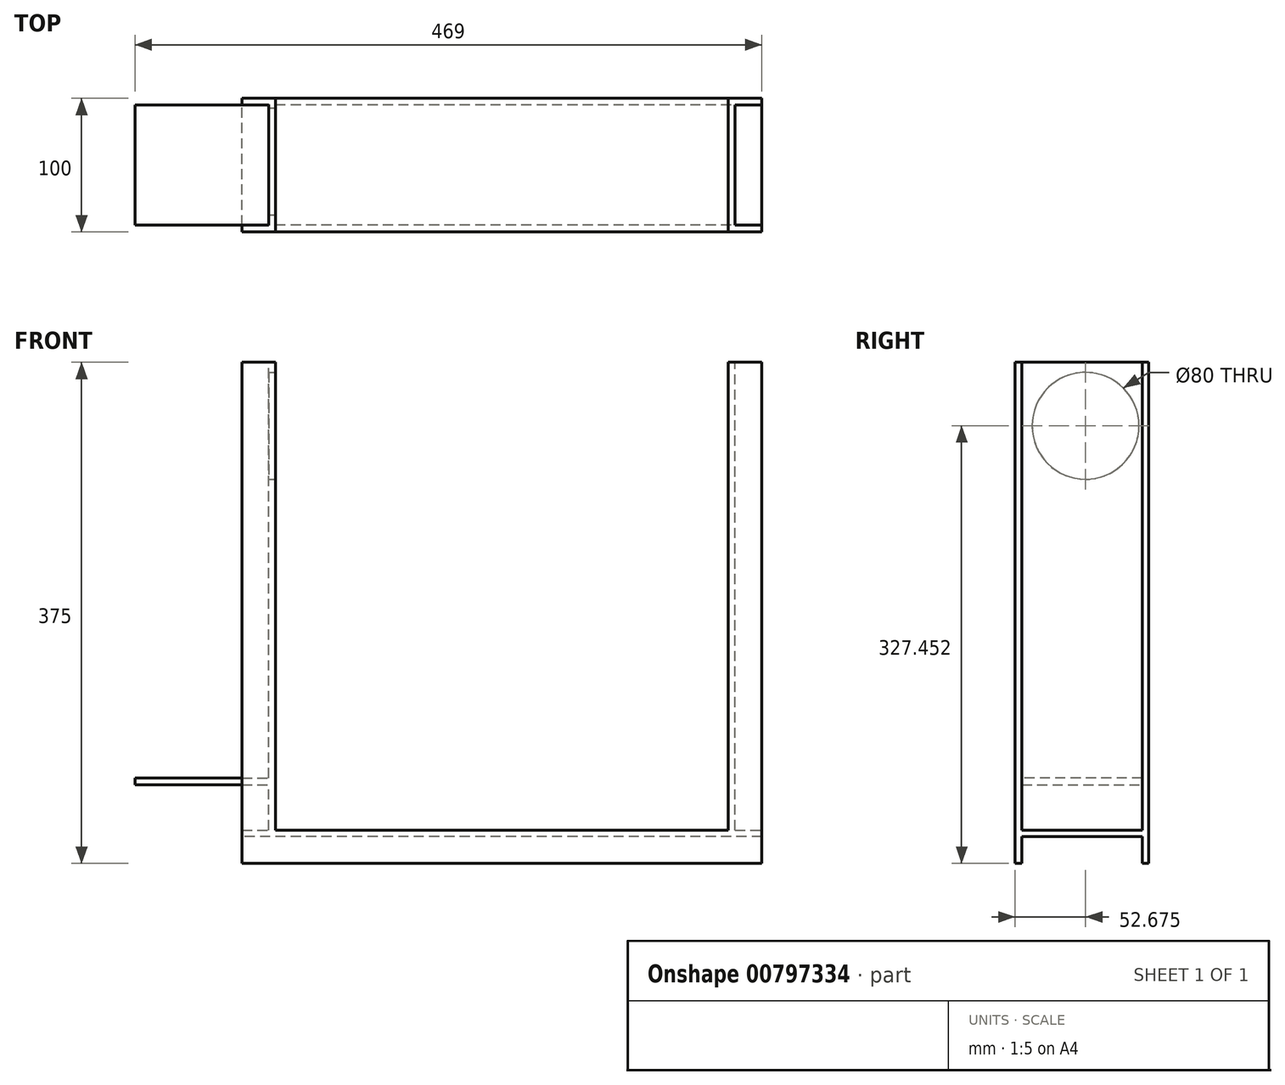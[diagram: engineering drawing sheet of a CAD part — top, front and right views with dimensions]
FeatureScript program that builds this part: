
annotation { "Feature Type Name" : "Feature", "Feature Type Description" : "" }
export const myFeature = defineFeature(function(context is Context, id is Id, definition is map)
    precondition{}
    {
        {
            var Q0;
            Q0=qCreatedBy(makeId("Front.planeOp"),FACE);
            var sketch = newSketch(context, id + "F0", { "sketchPlane" : qUnion([Q0])});
            skLineSegment(sketch, "E0", {"start": v(-205.4, 13.33) * mm, "end": v(-205.4, -6.67) * mm});
            skLineSegment(sketch, "E1", {"start": v(-205.4, -6.67) * mm, "end": v(183.6, -6.67) * mm});
            skLineSegment(sketch, "E2", {"start": v(183.6, -6.67) * mm, "end": v(183.6, 13.33) * mm});
            skLineSegment(sketch, "E3", {"start": v(-205.4, 13.33) * mm, "end": v(-205.4, 18.33) * mm});
            skLineSegment(sketch, "E4", {"start": v(-205.4, 18.33) * mm, "end": v(183.6, 18.33) * mm});
            skLineSegment(sketch, "E5", {"start": v(183.6, 18.33) * mm, "end": v(183.6, 13.33) * mm});
            skLineSegment(sketch, "E6", {"start": v(183.6, 13.33) * mm, "end": v(-205.4, 13.33) * mm});
            skLineSegment(sketch, "E7", {"start": v(-205.4, 18.33) * mm, "end": v(-180.4, 18.33) * mm});
            skLineSegment(sketch, "E8", {"start": v(-180.4, 18.33) * mm, "end": v(-180.4, 388.33) * mm});
            skLineSegment(sketch, "E9", {"start": v(-180.4, 388.33) * mm, "end": v(-205.4, 388.33) * mm});
            skLineSegment(sketch, "E10", {"start": v(-205.4, 388.33) * mm, "end": v(-205.4, 18.33) * mm});
            skLineSegment(sketch, "E11", {"start": v(-205.4, 18.33) * mm, "end": v(-185.4, 18.33) * mm});
            skLineSegment(sketch, "E12", {"start": v(-185.4, 18.33) * mm, "end": v(-185.4, 388.33) * mm});
            skLineSegment(sketch, "E13", {"start": v(183.6, 18.33) * mm, "end": v(183.6, 388.33) * mm});
            skLineSegment(sketch, "E14", {"start": v(183.6, 388.33) * mm, "end": v(163.6, 388.33) * mm});
            skLineSegment(sketch, "E15", {"start": v(163.6, 388.33) * mm, "end": v(158.6, 388.33) * mm});
            skLineSegment(sketch, "E16", {"start": v(158.6, 388.33) * mm, "end": v(158.6, 18.33) * mm});
            skLineSegment(sketch, "E17", {"start": v(158.6, 18.33) * mm, "end": v(163.6, 18.33) * mm});
            skLineSegment(sketch, "E18", {"start": v(163.6, 18.33) * mm, "end": v(163.6, 388.33) * mm});
            skSolve(sketch);
        }
        {
            var Q0;
            {var subQ3=sQuery(id+"F0.wireOp",EDGE,"E3");Q0=makeQuery(id+"F0.imprint","IMPRINT",FACE,{"disambiguationData":[TD([[makeQuery(id+"F0.imprint","IMPRINT",EDGE,{"derivedFrom":subQ3}),-1.0]])]});}
            var Q1;
            {var subQ0=sQuery(id+"F0.wireOp",EDGE,"E8");Q1=makeQuery(id+"F0.imprint","IMPRINT",FACE,{"disambiguationData":[TD([[makeQuery(id+"F0.imprint","IMPRINT",EDGE,{"derivedFrom":subQ0}),1.0]])]});}
            var Q2;
            Q2=makeQuery(id+"F0.imprint","IMPRINT",FACE,{"disambiguationData":[TD([[makeQuery(id+"F0.imprint","IMPRINT",EDGE,{"derivedFrom":sQuery(id+"F0.wireOp",EDGE,"E15")}),1.0]])]});
            extrude(context, id + "F1", {"entities" : qUnion([Q0, Q1, Q2]), "depth" : 100 * mm, "offsetDistance" : 25 * mm});
        }
        {
            var Q0;
            {var subQ0=sQuery(id+"F0.wireOp",EDGE,"E10");Q0=makeQuery(id+"F0.imprint","IMPRINT",FACE,{"disambiguationData":[TD([[makeQuery(id+"F0.imprint","IMPRINT",EDGE,{"derivedFrom":subQ0}),1.0]])]});}
            var Q1;
            Q1=makeQuery(id+"F0.imprint","IMPRINT",FACE,{"disambiguationData":[TD([[makeQuery(id+"F0.imprint","IMPRINT",EDGE,{"derivedFrom":sQuery(id+"F0.wireOp",EDGE,"E0")}),1.0]])]});
            var Q2;
            {var subQ2=sQuery(id+"F0.wireOp",EDGE,"E13");Q2=makeQuery(id+"F0.imprint","IMPRINT",FACE,{"disambiguationData":[TD([[makeQuery(id+"F0.imprint","IMPRINT",EDGE,{"derivedFrom":subQ2}),1.0]])]});}
            extrude(context, id + "F2", {"entities" : qUnion([Q0, Q1, Q2]), "operationType" : NewBodyOperationType.ADD, "depth" : 5 * mm, "offsetDistance" : 25 * mm});
        }
        {
            var Q0;
            Q0=makeQuery(id+"F1.opExtrude","CAP_FACE",FACE,{"disambiguationData":[OSD([sQuery(id+"F0.wireOp",EDGE,"E3"),sQuery(id+"F0.wireOp",EDGE,"E4"),sQuery(id+"F0.wireOp",EDGE,"E5"),sQuery(id+"F0.wireOp",EDGE,"E6"),sQuery(id+"F0.wireOp",EDGE,"E8"),sQuery(id+"F0.wireOp",EDGE,"E9"),sQuery(id+"F0.wireOp",EDGE,"E12"),sQuery(id+"F0.wireOp",EDGE,"E15"),sQuery(id+"F0.wireOp",EDGE,"E16"),sQuery(id+"F0.wireOp",EDGE,"E18")])],"isStart":false});
            var sketch = newSketch(context, id + "F3", { "sketchPlane" : qUnion([Q0])});
            skLineSegment(sketch, "E19", {"start": v(-185.4, 388.33) * mm, "end": v(-205.4, 388.33) * mm});
            skLineSegment(sketch, "E20", {"start": v(-205.4, 388.33) * mm, "end": v(-205.4, 18.33) * mm});
            skLineSegment(sketch, "E21", {"start": v(-205.4, 13.33) * mm, "end": v(-205.4, -6.67) * mm});
            skLineSegment(sketch, "E22", {"start": v(-205.4, -6.67) * mm, "end": v(183.6, -6.67) * mm});
            skLineSegment(sketch, "E23", {"start": v(183.6, -6.67) * mm, "end": v(183.6, 13.33) * mm});
            skLineSegment(sketch, "E24", {"start": v(163.6, 18.33) * mm, "end": v(183.6, 18.33) * mm});
            skLineSegment(sketch, "E25", {"start": v(163.6, 388.33) * mm, "end": v(183.6, 388.33) * mm});
            skLineSegment(sketch, "E26", {"start": v(183.6, 388.33) * mm, "end": v(183.6, 18.33) * mm});
            skSolve(sketch);
        }
        {
            var Q0;
            Q0=makeQuery(id+"F3.imprint","IMPRINT",FACE,{"disambiguationData":[TD([[makeQuery(id+"F3.imprint","IMPRINT",EDGE,{"derivedFrom":sQuery(id+"F3.wireOp",EDGE,"E19")}),1.0]])]});
            extrude(context, id + "F4", {"entities" : qUnion([Q0]), "operationType" : NewBodyOperationType.ADD, "oppositeDirection" : true, "depth" : 5 * mm, "offsetDistance" : 25 * mm});
        }
        {
            var Q0;
            Q0=makeQuery(id+"F3.imprint","IMPRINT",FACE,{"disambiguationData":[TD([[makeQuery(id+"F3.imprint","IMPRINT",EDGE,{"derivedFrom":sQuery(id+"F3.wireOp",EDGE,"E21")}),1.0]])]});
            var Q1;
            Q1=makeQuery(id+"F3.imprint","IMPRINT",FACE,{"disambiguationData":[TD([[makeQuery(id+"F3.imprint","IMPRINT",EDGE,{"derivedFrom":sQuery(id+"F3.wireOp",EDGE,"E24")}),1.0]])]});
            extrude(context, id + "F5", {"entities" : qUnion([Q0, Q1]), "operationType" : NewBodyOperationType.ADD, "oppositeDirection" : true, "depth" : 5 * mm, "offsetDistance" : 25 * mm});
        }
        {
            var Q0;
            Q0=makeQuery(id+"F1.opExtrude","SWEPT_FACE",FACE,{"disambiguationData":[OSD([sQuery(id+"F0.wireOp",EDGE,"E8")])]});
            var sketch = newSketch(context, id + "F6", { "sketchPlane" : qUnion([Q0])});
            skLineSegment(sketch, "E27", {"start": v(-100, 388.33) * mm, "end": v(-100, 363.33) * mm});
            skLineSegment(sketch, "E28", {"start": v(-100, 363.33) * mm, "end": v(0, 363.33) * mm});
            skLineSegment(sketch, "E29", {"start": v(2.85, 363.28) * mm, "end": v(-97.15, 363.28) * mm});
            skLineSegment(sketch, "E30", {"start": v(-97.15, 363.28) * mm, "end": v(-90, 363.28) * mm});
            skLineSegment(sketch, "E31", {"start": v(-90, 363.28) * mm, "end": v(-90, 278.28) * mm});
            skLineSegment(sketch, "E32", {"start": v(-90, 278.28) * mm, "end": v(-5, 278.28) * mm});
            skLineSegment(sketch, "E33", {"start": v(-5, 278.28) * mm, "end": v(-5, 363.28) * mm});
            skLineSegment(sketch, "E34", {"start": v(-90, 363.28) * mm, "end": v(-81.7, 363.28) * mm});
            skLineSegment(sketch, "E35", {"start": v(-81.7, 363.28) * mm, "end": v(-81.7, 354.98) * mm});
            skCircle(sketch, "E36", {"center": v(-81.7, 354.98) * mm, "radius": 3.27 * mm});
            skLineSegment(sketch, "E37", {"start": v(-81.7, 363.28) * mm, "end": v(-81.7, 278.28) * mm});
            skLineSegment(sketch, "E38", {"start": v(-81.7, 278.28) * mm, "end": v(-81.7, 286.58) * mm});
            skLineSegment(sketch, "E39", {"start": v(-81.7, 286.58) * mm, "end": v(-5, 286.58) * mm});
            skLineSegment(sketch, "E40", {"start": v(-5, 363.28) * mm, "end": v(-13.3, 363.28) * mm});
            skLineSegment(sketch, "E41", {"start": v(-13.3, 363.28) * mm, "end": v(-13.3, 278.28) * mm});
            skLineSegment(sketch, "E42", {"start": v(-90, 354.98) * mm, "end": v(-13.3, 354.98) * mm});
            skCircle(sketch, "E43", {"center": v(-13.3, 354.98) * mm, "radius": 3.27 * mm});
            skCircle(sketch, "E44", {"center": v(-81.7, 286.58) * mm, "radius": 3.27 * mm});
            skCircle(sketch, "E45", {"center": v(-13.3, 286.58) * mm, "radius": 3.27 * mm});
            skLineSegment(sketch, "E46", {"start": v(-90, 320.78) * mm, "end": v(-13.3, 320.78) * mm});
            skLineSegment(sketch, "E47", {"start": v(-47.15, 363.28) * mm, "end": v(-47.5, 278.28) * mm});
            skCircle(sketch, "E48", {"center": v(-47.33, 320.78) * mm, "radius": 6.25 * mm});
            skLineSegment(sketch, "E49", {"start": v(-90, 278.28) * mm, "end": v(-100, 278.28) * mm});
            skLineSegment(sketch, "E50", {"start": v(-100, 278.28) * mm, "end": v(0, 278.28) * mm});
            skLineSegment(sketch, "E51", {"start": v(0, 363.33) * mm, "end": v(0, 368.33) * mm});
            skLineSegment(sketch, "E52", {"start": v(0, 368.33) * mm, "end": v(-100, 368.33) * mm});
            skLineSegment(sketch, "E53", {"start": v(0, 368.33) * mm, "end": v(0, 388.33) * mm});
            skLineSegment(sketch, "E54", {"start": v(0, 278.28) * mm, "end": v(0, 273.28) * mm});
            skLineSegment(sketch, "E55", {"start": v(0, 273.28) * mm, "end": v(-100, 273.28) * mm});
            skLineSegment(sketch, "E56", {"start": v(-97.15, 363.28) * mm, "end": v(-92.15, 363.28) * mm});
            skLineSegment(sketch, "E57", {"start": v(0, 388.33) * mm, "end": v(-5, 388.33) * mm});
            skLineSegment(sketch, "E58", {"start": v(-5, 388.33) * mm, "end": v(-5, 368.33) * mm});
            skLineSegment(sketch, "E59", {"start": v(0, 273.28) * mm, "end": v(-2.6, 273.28) * mm});
            skLineSegment(sketch, "E60", {"start": v(-100, 278.28) * mm, "end": v(-95, 278.28) * mm});
            skLineSegment(sketch, "E61", {"start": v(0, 273.28) * mm, "end": v(-5, 273.28) * mm});
            skLineSegment(sketch, "E62", {"start": v(-100, 363.33) * mm, "end": v(-94.65, 343.18) * mm});
            skLineSegment(sketch, "E63", {"start": v(-100, 388.33) * mm, "end": v(-95, 388.33) * mm});
            skLineSegment(sketch, "E64", {"start": v(-95, 388.33) * mm, "end": v(-95, 363.33) * mm});
            skCircle(sketch, "E65", {"center": v(-47.33, 320.78) * mm, "radius": 40 * mm});
            skSolve(sketch);
        }
        {
            var Q0;
            Q0=makeQuery(id+"F5.boolean.opBoolean","MERGE",FACE,{"derivedFrom":[makeQuery(id+"F2.boolean.opBoolean","MERGE",FACE,{"derivedFrom":[makeQuery(id+"F1.opExtrude","SWEPT_FACE",FACE,{"disambiguationData":[OSD([sQuery(id+"F0.wireOp",EDGE,"E15")])]}),makeQuery(id+"F2.opExtrude","SWEPT_FACE",FACE,{"disambiguationData":[OSD([sQuery(id+"F0.wireOp",EDGE,"E14")])]})]}),makeQuery(id+"F5.opExtrude","SWEPT_FACE",FACE,{"disambiguationData":[OSD([sQuery(id+"F3.wireOp",EDGE,"E25")])]})]});
            extrude(context, id + "F7", {"entities" : qUnion([Q0]), "operationType" : NewBodyOperationType.REMOVE, "oppositeDirection" : true, "depth" : 20 * mm, "offsetDistance" : 25 * mm});
        }
        {
            var Q0;
            {var subQ5=sQuery(id+"F6.wireOp",EDGE,"E65");var subQ8=sQuery(id+"F6.wireOp",EDGE,"E37");var subQ11=makeQuery(id+"F6.imprint","INTERSECT",VERTEX,{"disambiguationData":[OD(0.0)],"derivedFrom":[subQ8,subQ5]});Q0=makeQuery(id+"F6.imprint","IMPRINT",FACE,{"disambiguationData":[TD([[makeQuery(id+"F6.imprint","IMPRINT",EDGE,{"disambiguationData":[TD([[subQ11,-1.0]])],"derivedFrom":subQ8}),1.0]])]});}
            var Q1;
            {var subQ0=sQuery(id+"F6.wireOp",EDGE,"E65");var subQ1=sQuery(id+"F6.wireOp",EDGE,"E37");var subQ2=makeQuery(id+"F6.imprint","INTERSECT",VERTEX,{"disambiguationData":[OD(0.0)],"derivedFrom":[subQ1,subQ0]});Q1=makeQuery(id+"F6.imprint","IMPRINT",FACE,{"disambiguationData":[TD([[makeQuery(id+"F6.imprint","IMPRINT",EDGE,{"disambiguationData":[TD([[subQ2,-1.0]])],"derivedFrom":subQ1}),-1.0]])]});}
            var Q2;
            {var subQ0=sQuery(id+"F6.wireOp",EDGE,"E46");var subQ1=sQuery(id+"F6.wireOp",EDGE,"E37");var subQ2=makeQuery(id+"F6.imprint","INTERSECT",VERTEX,{"derivedFrom":[subQ1,subQ0]});Q2=makeQuery(id+"F6.imprint","IMPRINT",FACE,{"disambiguationData":[TD([[makeQuery(id+"F6.imprint","IMPRINT",EDGE,{"disambiguationData":[TD([[subQ2,-1.0]])],"derivedFrom":subQ1}),-1.0]])]});}
            var Q3;
            {var subQ0=sQuery(id+"F6.wireOp",EDGE,"E41");var subQ1=makeQuery(id+"F6.imprint","INTERSECT",VERTEX,{"derivedFrom":[subQ0,sQuery(id+"F6.wireOp",EDGE,"E46")]});Q3=makeQuery(id+"F6.imprint","IMPRINT",FACE,{"disambiguationData":[TD([[makeQuery(id+"F6.imprint","IMPRINT",EDGE,{"disambiguationData":[TD([[subQ1,1.0]])],"derivedFrom":subQ0}),1.0]])]});}
            var Q4;
            {var subQ7=sQuery(id+"F6.wireOp",EDGE,"E47");var subQ8=sQuery(id+"F6.wireOp",EDGE,"E39");var subQ9=makeQuery(id+"F6.imprint","INTERSECT",VERTEX,{"derivedFrom":[subQ8,subQ7]});Q4=makeQuery(id+"F6.imprint","IMPRINT",FACE,{"disambiguationData":[TD([[makeQuery(id+"F6.imprint","IMPRINT",EDGE,{"disambiguationData":[TD([[subQ9,-1.0]])],"derivedFrom":subQ8}),1.0]])]});}
            var Q5;
            {var subQ5=sQuery(id+"F6.wireOp",EDGE,"E46");var subQ6=sQuery(id+"F6.wireOp",EDGE,"E41");var subQ7=makeQuery(id+"F6.imprint","INTERSECT",VERTEX,{"derivedFrom":[subQ6,subQ5]});Q5=makeQuery(id+"F6.imprint","IMPRINT",FACE,{"disambiguationData":[TD([[makeQuery(id+"F6.imprint","IMPRINT",EDGE,{"disambiguationData":[TD([[subQ7,1.0]])],"derivedFrom":subQ6}),-1.0]])]});}
            var Q6;
            {var subQ5=sQuery(id+"F6.wireOp",EDGE,"E46");var subQ6=sQuery(id+"F6.wireOp",EDGE,"E37");var subQ7=makeQuery(id+"F6.imprint","INTERSECT",VERTEX,{"derivedFrom":[subQ6,subQ5]});Q6=makeQuery(id+"F6.imprint","IMPRINT",FACE,{"disambiguationData":[TD([[makeQuery(id+"F6.imprint","IMPRINT",EDGE,{"disambiguationData":[TD([[subQ7,-1.0]])],"derivedFrom":subQ6}),1.0]])]});}
            var Q7;
            {var subQ0=sQuery(id+"F6.wireOp",EDGE,"E65");var subQ1=sQuery(id+"F6.wireOp",EDGE,"E39");var subQ2=makeQuery(id+"F6.imprint","INTERSECT",VERTEX,{"disambiguationData":[OD(0.0)],"derivedFrom":[subQ1,subQ0]});Q7=makeQuery(id+"F6.imprint","IMPRINT",FACE,{"disambiguationData":[TD([[makeQuery(id+"F6.imprint","IMPRINT",EDGE,{"disambiguationData":[TD([[subQ2,-1.0]])],"derivedFrom":subQ1}),-1.0]])]});}
            var Q8;
            {var subQ0=sQuery(id+"F6.wireOp",EDGE,"E47");var subQ1=sQuery(id+"F6.wireOp",EDGE,"E39");var subQ2=makeQuery(id+"F6.imprint","INTERSECT",VERTEX,{"derivedFrom":[subQ1,subQ0]});Q8=makeQuery(id+"F6.imprint","IMPRINT",FACE,{"disambiguationData":[TD([[makeQuery(id+"F6.imprint","IMPRINT",EDGE,{"disambiguationData":[TD([[subQ2,-1.0]])],"derivedFrom":subQ1}),-1.0]])]});}
            var Q9;
            {var subQ0=sQuery(id+"F6.wireOp",EDGE,"E48");var subQ1=sQuery(id+"F6.wireOp",EDGE,"E46");var subQ2=makeQuery(id+"F6.imprint","INTERSECT",VERTEX,{"disambiguationData":[OD(0.0)],"derivedFrom":[subQ1,subQ0]});Q9=makeQuery(id+"F6.imprint","IMPRINT",FACE,{"disambiguationData":[TD([[makeQuery(id+"F6.imprint","IMPRINT",EDGE,{"disambiguationData":[TD([[subQ2,-1.0]])],"derivedFrom":subQ1}),-1.0]])]});}
            var Q10;
            {var subQ0=sQuery(id+"F6.wireOp",EDGE,"E48");var subQ1=sQuery(id+"F6.wireOp",EDGE,"E46");var subQ2=makeQuery(id+"F6.imprint","INTERSECT",VERTEX,{"disambiguationData":[OD(0.0)],"derivedFrom":[subQ1,subQ0]});Q10=makeQuery(id+"F6.imprint","IMPRINT",FACE,{"disambiguationData":[TD([[makeQuery(id+"F6.imprint","IMPRINT",EDGE,{"disambiguationData":[TD([[subQ2,-1.0]])],"derivedFrom":subQ1}),1.0]])]});}
            var Q11;
            {var subQ0=sQuery(id+"F6.wireOp",EDGE,"E47");var subQ1=sQuery(id+"F6.wireOp",EDGE,"E46");var subQ2=makeQuery(id+"F6.imprint","INTERSECT",VERTEX,{"derivedFrom":[subQ1,subQ0]});Q11=makeQuery(id+"F6.imprint","IMPRINT",FACE,{"disambiguationData":[TD([[makeQuery(id+"F6.imprint","IMPRINT",EDGE,{"disambiguationData":[TD([[subQ2,-1.0]])],"derivedFrom":subQ1}),1.0]])]});}
            var Q12;
            {var subQ0=sQuery(id+"F6.wireOp",EDGE,"E47");var subQ1=sQuery(id+"F6.wireOp",EDGE,"E46");var subQ2=makeQuery(id+"F6.imprint","INTERSECT",VERTEX,{"derivedFrom":[subQ1,subQ0]});Q12=makeQuery(id+"F6.imprint","IMPRINT",FACE,{"disambiguationData":[TD([[makeQuery(id+"F6.imprint","IMPRINT",EDGE,{"disambiguationData":[TD([[subQ2,-1.0]])],"derivedFrom":subQ1}),-1.0]])]});}
            var Q13;
            {var subQ0=sQuery(id+"F6.wireOp",EDGE,"E65");var subQ1=sQuery(id+"F6.wireOp",EDGE,"E42");var subQ2=makeQuery(id+"F6.imprint","INTERSECT",VERTEX,{"disambiguationData":[OD(0.0)],"derivedFrom":[subQ1,subQ0]});Q13=makeQuery(id+"F6.imprint","IMPRINT",FACE,{"disambiguationData":[TD([[makeQuery(id+"F6.imprint","IMPRINT",EDGE,{"disambiguationData":[TD([[subQ2,-1.0]])],"derivedFrom":subQ1}),1.0]])]});}
            var Q14;
            {var subQ0=sQuery(id+"F6.wireOp",EDGE,"E47");var subQ1=sQuery(id+"F6.wireOp",EDGE,"E42");var subQ2=makeQuery(id+"F6.imprint","INTERSECT",VERTEX,{"derivedFrom":[subQ1,subQ0]});Q14=makeQuery(id+"F6.imprint","IMPRINT",FACE,{"disambiguationData":[TD([[makeQuery(id+"F6.imprint","IMPRINT",EDGE,{"disambiguationData":[TD([[subQ2,-1.0]])],"derivedFrom":subQ1}),1.0]])]});}
            extrude(context, id + "F8", {"entities" : qUnion([Q0, Q1, Q2, Q3, Q4, Q5, Q6, Q7, Q8, Q9, Q10, Q11, Q12, Q13, Q14]), "operationType" : NewBodyOperationType.REMOVE, "oppositeDirection" : true, "depth" : 25 * mm, "offsetDistance" : 25 * mm});
        }
        {
            var Q0;
            Q0=makeQuery(id+"F1.opExtrude","SWEPT_FACE",FACE,{"disambiguationData":[OSD([sQuery(id+"F0.wireOp",EDGE,"E12")])]});
            var sketch = newSketch(context, id + "F9", { "sketchPlane" : qUnion([Q0])});
            skLineSegment(sketch, "E66", {"start": v(87.32, 321.33) * mm, "end": v(87.32, 101.33) * mm});
            skLineSegment(sketch, "E67", {"start": v(87.32, 101.33) * mm, "end": v(5, 101.33) * mm});
            skLineSegment(sketch, "E68", {"start": v(5, 101.33) * mm, "end": v(95, 101.33) * mm});
            skLineSegment(sketch, "E69", {"start": v(95, 101.33) * mm, "end": v(95, 96.33) * mm});
            skLineSegment(sketch, "E70", {"start": v(95, 96.33) * mm, "end": v(5, 96.33) * mm});
            skLineSegment(sketch, "E71", {"start": v(50, 96.33) * mm, "end": v(50, 18.33) * mm});
            skLineSegment(sketch, "E72", {"start": v(50, 18.33) * mm, "end": v(50, 57.33) * mm});
            skLineSegment(sketch, "E73", {"start": v(50, 57.33) * mm, "end": v(95, 57.33) * mm});
            skLineSegment(sketch, "E74", {"start": v(95, 57.33) * mm, "end": v(95, 52.33) * mm});
            skLineSegment(sketch, "E75", {"start": v(95, 52.33) * mm, "end": v(5, 52.33) * mm});
            skLineSegment(sketch, "E76", {"start": v(50, 57.33) * mm, "end": v(5, 57.33) * mm});
            skSolve(sketch);
        }
        {
            var Q0;
            {var subQ0=sQuery(id+"F0.wireOp",EDGE,"E9");Q0=makeQuery(id+"F4.boolean.opBoolean","MERGE",FACE,{"derivedFrom":[makeQuery(id+"F2.boolean.opBoolean","MERGE",FACE,{"derivedFrom":[makeQuery(id+"F1.opExtrude","SWEPT_FACE",FACE,{"disambiguationData":[OSD([subQ0])]}),makeQuery(id+"F2.opExtrude","SWEPT_FACE",FACE,{"disambiguationData":[OSD([subQ0])]})]}),makeQuery(id+"F4.opExtrude","SWEPT_FACE",FACE,{"disambiguationData":[OSD([sQuery(id+"F3.wireOp",EDGE,"E19")])]})]});}
            extrude(context, id + "F10", {"entities" : qUnion([Q0]), "operationType" : NewBodyOperationType.REMOVE, "oppositeDirection" : true, "depth" : 20 * mm, "offsetDistance" : 25 * mm});
        }
        {
            var Q0;
            Q0 = qSketchRegion(id + "F9", true);
            var Q1;
            {var subQ0=sQuery(id+"F9.wireOp",EDGE,"E76");Q1=makeQuery(id+"F9.imprint","IMPRINT",FACE,{"disambiguationData":[TD([[makeQuery(id+"F9.imprint","IMPRINT",EDGE,{"derivedFrom":subQ0}),1.0]])]});}
            extrude(context, id + "F11", {"entities" : qUnion([Q0, Q1]), "operationType" : NewBodyOperationType.ADD, "depth" : 100 * mm, "offsetDistance" : 25 * mm});
        }
    });
